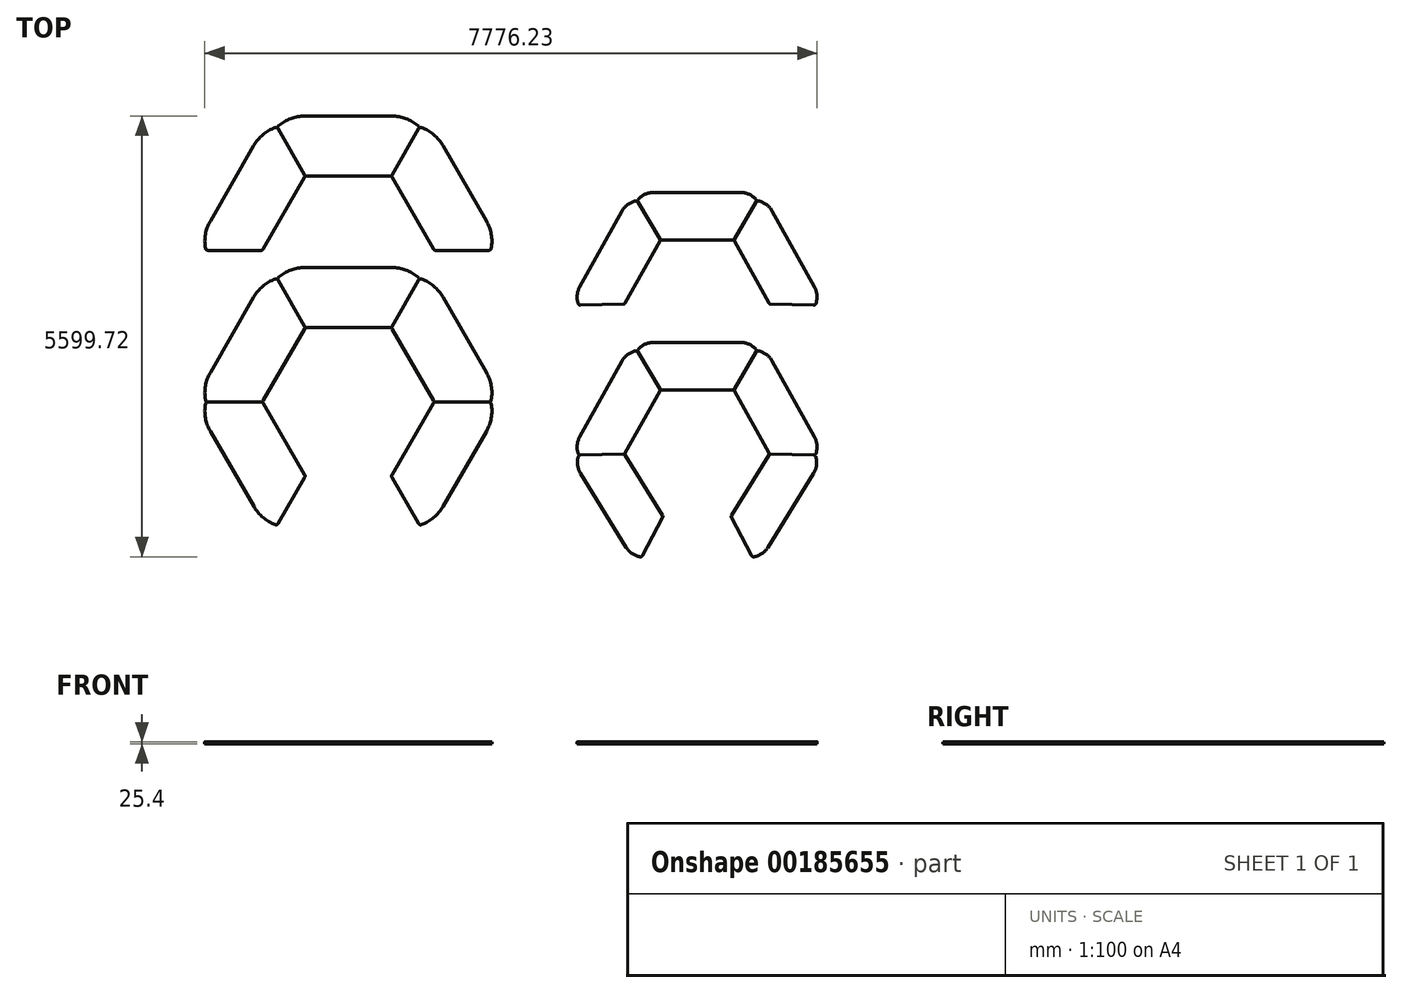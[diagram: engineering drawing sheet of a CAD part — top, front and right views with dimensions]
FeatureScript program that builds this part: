
annotation { "Feature Type Name" : "Feature", "Feature Type Description" : "" }
export const myFeature = defineFeature(function(context is Context, id is Id, definition is map)
    precondition{}
    {
        {
            var Q0;
            Q0=qCreatedBy(makeId("Top.planeOp"),FACE);
            var sketch = newSketch(context, id + "F0", { "sketchPlane" : qUnion([Q0])});
            skLineSegment(sketch, "E0", {"start": v(-1070.65, -55.75) * mm, "end": v(-16.67, -55.75) * mm});
            skLineSegment(sketch, "E1", {"start": v(-1436.4, 546.82) * mm, "end": v(-1097.33, -40.35) * mm});
            skLineSegment(sketch, "E2", {"start": v(10, -40.35) * mm, "end": v(349.27, 547.15) * mm});
            skLineSegment(sketch, "E3", {"start": v(-543.66, 584.33) * mm, "end": v(-543.66, -55.75) * mm});
            skPoint(sketch, "E4.visualSharp", {"position": v(-1088.43, -55.75) * mm});
            skArc(sketch, "E4.filletArc", {"start": v(-1097.33, -40.35) * mm, "mid": v(-1086.05, -51.62) * mm, "end": v(-1070.65, -55.75) * mm});
            skPoint(sketch, "E5.visualSharp", {"position": v(1.11, -55.75) * mm});
            skArc(sketch, "E5.filletArc", {"start": v(-16.67, -55.75) * mm, "mid": v(-1.27, -51.62) * mm, "end": v(10, -40.35) * mm});
            skLineSegment(sketch, "E6", {"start": v(-543.66, -55.75) * mm, "end": v(-543.66, 706.25) * mm});
            skPoint(sketch, "E7.visualSharp", {"position": v(8.73, 706.25) * mm});
            skLineSegment(sketch, "E8", {"start": v(-1096.05, 706.25) * mm, "end": v(8.73, 706.25) * mm});
            skArc(sketch, "E9", {"start": v(-1096.05, 706.25) * mm, "mid": v(-1273.45, 675.07) * mm, "end": v(-1429.58, 585.26) * mm});
            skArc(sketch, "E10", {"start": v(342.4, 585.63) * mm, "mid": v(186.13, 675.17) * mm, "end": v(8.73, 706.25) * mm});
            skPoint(sketch, "E11.visualSharp", {"position": v(361.73, 568.73) * mm});
            skArc(sketch, "E11.filletArc", {"start": v(349.27, 547.15) * mm, "mid": v(352.86, 567.65) * mm, "end": v(342.4, 585.63) * mm});
            skPoint(sketch, "E12.visualSharp", {"position": v(-1448.84, 568.35) * mm});
            skArc(sketch, "E12.filletArc", {"start": v(-1429.58, 585.26) * mm, "mid": v(-1440, 567.29) * mm, "end": v(-1436.4, 546.82) * mm});
            skSolve(sketch);
        }
        {
            var Q0;
            {var subQ1=sQuery(id+"F0.wireOp",EDGE,"E1");Q0=makeQuery(id+"F0.imprint","IMPRINT",FACE,{"disambiguationData":[TD([[makeQuery(id+"F0.imprint","IMPRINT",EDGE,{"derivedFrom":subQ1}),1.0]])]});}
            var Q1;
            {var subQ1=sQuery(id+"F0.wireOp",EDGE,"E2");Q1=makeQuery(id+"F0.imprint","IMPRINT",FACE,{"disambiguationData":[TD([[makeQuery(id+"F0.imprint","IMPRINT",EDGE,{"derivedFrom":subQ1}),1.0]])]});}
            extrude(context, id + "F1", {"entities" : qUnion([Q0, Q1]), "depth" : 25.4 * mm});
        }
        {
            var Q0;
            Q0=makeQuery(id+"F1.opExtrude","SWEPT_BODY",BODY,{"disambiguationData":[OSD([sQuery(id+"F0.wireOp",EDGE,"1ubpbm2j-zJwo-eIPi-8dKW-a2tcgGCZGCWk"),sQuery(id+"F0.wireOp",EDGE,"E0"),sQuery(id+"F0.wireOp",EDGE,"E1"),sQuery(id+"F0.wireOp",EDGE,"E2"),sQuery(id+"F0.wireOp",EDGE,"E4.filletArc"),sQuery(id+"F0.wireOp",EDGE,"E5.filletArc")])]});
            var Q1;
            Q1=makeQuery(id+"F1.opExtrude","SWEPT_FACE",FACE,{"disambiguationData":[OSD([sQuery(id+"F0.wireOp",EDGE,"E1")])]});
            mirror(context, id + "F2", {"entities" : qUnion([Q0]), "mirrorPlane" : qUnion([Q1])});
        }
        {
            var Q0;
            Q0=makeQuery(id+"F1.opExtrude","SWEPT_BODY",BODY,{"disambiguationData":[OSD([sQuery(id+"F0.wireOp",EDGE,"1ubpbm2j-zJwo-eIPi-8dKW-a2tcgGCZGCWk"),sQuery(id+"F0.wireOp",EDGE,"E0"),sQuery(id+"F0.wireOp",EDGE,"E1"),sQuery(id+"F0.wireOp",EDGE,"E2"),sQuery(id+"F0.wireOp",EDGE,"E4.filletArc"),sQuery(id+"F0.wireOp",EDGE,"E5.filletArc")])]});
            var Q1;
            Q1=makeQuery(id+"F1.opExtrude","SWEPT_FACE",FACE,{"disambiguationData":[OSD([sQuery(id+"F0.wireOp",EDGE,"E2")])]});
            mirror(context, id + "F3", {"entities" : qUnion([Q0]), "mirrorPlane" : qUnion([Q1])});
        }
        {
            var Q0;
            Q0=makeQuery(id+"F1.opExtrude","SWEPT_BODY",BODY,{"disambiguationData":[OSD([sQuery(id+"F0.wireOp",EDGE,"1ubpbm2j-zJwo-eIPi-8dKW-a2tcgGCZGCWk"),sQuery(id+"F0.wireOp",EDGE,"E0"),sQuery(id+"F0.wireOp",EDGE,"E1"),sQuery(id+"F0.wireOp",EDGE,"E2"),sQuery(id+"F0.wireOp",EDGE,"E4.filletArc"),sQuery(id+"F0.wireOp",EDGE,"E5.filletArc")])]});
            transform(context, id + "F4", {"entities" : qUnion([Q0]), "transformType" : TransformType.TRANSLATION_3D, "dx" : 0 * mm, "dy" : -1925.32 * mm, "dz" : 0 * mm, "makeCopy" : true});
        }
        {
            var Q0;
            Q0=makeQuery(id+"F4.opPattern","COPY",BODY,{"derivedFrom":makeQuery(id+"F1.opExtrude","SWEPT_BODY",BODY,{"disambiguationData":[OSD([sQuery(id+"F0.wireOp",EDGE,"1ubpbm2j-zJwo-eIPi-8dKW-a2tcgGCZGCWk"),sQuery(id+"F0.wireOp",EDGE,"E0"),sQuery(id+"F0.wireOp",EDGE,"E1"),sQuery(id+"F0.wireOp",EDGE,"E2"),sQuery(id+"F0.wireOp",EDGE,"E4.filletArc"),sQuery(id+"F0.wireOp",EDGE,"E5.filletArc")])]}),"instanceName":"1"});
            var Q1;
            Q1=makeQuery(id+"F4.opPattern","COPY",FACE,{"derivedFrom":makeQuery(id+"F1.opExtrude","SWEPT_FACE",FACE,{"disambiguationData":[OSD([sQuery(id+"F0.wireOp",EDGE,"E1")])]}),"instanceName":"1"});
            mirror(context, id + "F5", {"entities" : qUnion([Q0]), "mirrorPlane" : qUnion([Q1])});
        }
        {
            var Q0;
            Q0=makeQuery(id+"F5.opPattern","COPY",BODY,{"derivedFrom":makeQuery(id+"F4.opPattern","COPY",BODY,{"derivedFrom":makeQuery(id+"F1.opExtrude","SWEPT_BODY",BODY,{"disambiguationData":[OSD([sQuery(id+"F0.wireOp",EDGE,"1ubpbm2j-zJwo-eIPi-8dKW-a2tcgGCZGCWk"),sQuery(id+"F0.wireOp",EDGE,"E0"),sQuery(id+"F0.wireOp",EDGE,"E1"),sQuery(id+"F0.wireOp",EDGE,"E2"),sQuery(id+"F0.wireOp",EDGE,"E4.filletArc"),sQuery(id+"F0.wireOp",EDGE,"E5.filletArc")])]}),"instanceName":"1"}),"instanceName":"1"});
            var Q1;
            Q1=makeQuery(id+"F5.opPattern","COPY",FACE,{"derivedFrom":makeQuery(id+"F4.opPattern","COPY",FACE,{"derivedFrom":makeQuery(id+"F1.opExtrude","SWEPT_FACE",FACE,{"disambiguationData":[OSD([sQuery(id+"F0.wireOp",EDGE,"E2")])]}),"instanceName":"1"}),"instanceName":"1"});
            mirror(context, id + "F6", {"entities" : qUnion([Q0]), "mirrorPlane" : qUnion([Q1])});
        }
        {
            var Q0;
            Q0=qCreatedBy(makeId("Top.planeOp"),FACE);
            var sketch = newSketch(context, id + "F7", { "sketchPlane" : qUnion([Q0])});
            skLineSegment(sketch, "E13", {"start": v(3434.2, -869.87) * mm, "end": v(4337.07, -869.87) * mm});
            skLineSegment(sketch, "E14", {"start": v(3135.74, -386.36) * mm, "end": v(3412.3, -857.33) * mm});
            skLineSegment(sketch, "E15", {"start": v(4358.97, -857.33) * mm, "end": v(4635.53, -386.36) * mm});
            skPoint(sketch, "E16.visualSharp", {"position": v(3419.66, -869.87) * mm});
            skArc(sketch, "E16.filletArc", {"start": v(3412.3, -857.33) * mm, "mid": v(3421.58, -866.51) * mm, "end": v(3434.2, -869.87) * mm});
            skPoint(sketch, "E17.visualSharp", {"position": v(4351.6, -869.87) * mm});
            skArc(sketch, "E17.filletArc", {"start": v(4337.07, -869.87) * mm, "mid": v(4349.69, -866.51) * mm, "end": v(4358.97, -857.33) * mm});
            skLineSegment(sketch, "E18", {"start": v(3885.63, -365.75) * mm, "end": v(3885.63, -869.87) * mm});
            skLineSegment(sketch, "E19", {"start": v(3885.63, -869.87) * mm, "end": v(3885.63, -264.43) * mm});
            skLineSegment(sketch, "E20", {"start": v(3333.25, -264.43) * mm, "end": v(4438.02, -264.43) * mm});
            skArc(sketch, "E21", {"start": v(3333.25, -264.43) * mm, "mid": v(3227.14, -286.97) * mm, "end": v(3139.36, -350.7) * mm});
            skArc(sketch, "E22", {"start": v(4631.9, -350.7) * mm, "mid": v(4544.12, -286.97) * mm, "end": v(4438.02, -264.43) * mm});
            skPoint(sketch, "E23.visualSharp", {"position": v(3125, -368.08) * mm});
            skArc(sketch, "E23.filletArc", {"start": v(3139.36, -350.7) * mm, "mid": v(3131.72, -367.94) * mm, "end": v(3135.74, -386.36) * mm});
            skPoint(sketch, "E24.visualSharp", {"position": v(4646.26, -368.08) * mm});
            skArc(sketch, "E24.filletArc", {"start": v(4635.53, -386.36) * mm, "mid": v(4639.55, -367.94) * mm, "end": v(4631.9, -350.7) * mm});
            skSolve(sketch);
        }
        {
            var Q0;
            {var subQ1=sQuery(id+"F7.wireOp",EDGE,"E15");Q0=makeQuery(id+"F7.imprint","IMPRINT",FACE,{"disambiguationData":[TD([[makeQuery(id+"F7.imprint","IMPRINT",EDGE,{"derivedFrom":subQ1}),1.0]])]});}
            var Q1;
            {var subQ1=sQuery(id+"F7.wireOp",EDGE,"E14");Q1=makeQuery(id+"F7.imprint","IMPRINT",FACE,{"disambiguationData":[TD([[makeQuery(id+"F7.imprint","IMPRINT",EDGE,{"derivedFrom":subQ1}),1.0]])]});}
            extrude(context, id + "F8", {"entities" : qUnion([Q0, Q1]), "depth" : 25.4 * mm});
        }
        {
            var Q0;
            Q0=makeQuery(id+"F8.opExtrude","SWEPT_BODY",BODY,{"disambiguationData":[OSD([sQuery(id+"F7.wireOp",EDGE,"pXNZPhRm-cwQ2-fNh0-WMuh-DQMg4mvni5s0"),sQuery(id+"F7.wireOp",EDGE,"E13"),sQuery(id+"F7.wireOp",EDGE,"E14"),sQuery(id+"F7.wireOp",EDGE,"E15"),sQuery(id+"F7.wireOp",EDGE,"E16.filletArc"),sQuery(id+"F7.wireOp",EDGE,"E17.filletArc")])]});
            var Q1;
            Q1=makeQuery(id+"F8.opExtrude","SWEPT_FACE",FACE,{"disambiguationData":[OSD([sQuery(id+"F7.wireOp",EDGE,"E14")])]});
            mirror(context, id + "F9", {"entities" : qUnion([Q0]), "mirrorPlane" : qUnion([Q1])});
        }
        {
            var Q0;
            Q0=makeQuery(id+"F8.opExtrude","SWEPT_BODY",BODY,{"disambiguationData":[OSD([sQuery(id+"F7.wireOp",EDGE,"pXNZPhRm-cwQ2-fNh0-WMuh-DQMg4mvni5s0"),sQuery(id+"F7.wireOp",EDGE,"E13"),sQuery(id+"F7.wireOp",EDGE,"E14"),sQuery(id+"F7.wireOp",EDGE,"E15"),sQuery(id+"F7.wireOp",EDGE,"E16.filletArc"),sQuery(id+"F7.wireOp",EDGE,"E17.filletArc")])]});
            var Q1;
            Q1=makeQuery(id+"F8.opExtrude","SWEPT_FACE",FACE,{"disambiguationData":[OSD([sQuery(id+"F7.wireOp",EDGE,"E15")])]});
            mirror(context, id + "F10", {"entities" : qUnion([Q0]), "mirrorPlane" : qUnion([Q1])});
        }
        {
            var Q0;
            Q0=makeQuery(id+"F8.opExtrude","SWEPT_BODY",BODY,{"disambiguationData":[OSD([sQuery(id+"F7.wireOp",EDGE,"pXNZPhRm-cwQ2-fNh0-WMuh-DQMg4mvni5s0"),sQuery(id+"F7.wireOp",EDGE,"E13"),sQuery(id+"F7.wireOp",EDGE,"E14"),sQuery(id+"F7.wireOp",EDGE,"E15"),sQuery(id+"F7.wireOp",EDGE,"E16.filletArc"),sQuery(id+"F7.wireOp",EDGE,"E17.filletArc")])]});
            transform(context, id + "F11", {"entities" : qUnion([Q0]), "transformType" : TransformType.TRANSLATION_3D, "dx" : 0 * mm, "dy" : -1905 * mm, "dz" : 0 * mm, "makeCopy" : true});
        }
        {
            var Q0;
            Q0=makeQuery(id+"F11.opPattern","COPY",BODY,{"derivedFrom":makeQuery(id+"F8.opExtrude","SWEPT_BODY",BODY,{"disambiguationData":[OSD([sQuery(id+"F7.wireOp",EDGE,"pXNZPhRm-cwQ2-fNh0-WMuh-DQMg4mvni5s0"),sQuery(id+"F7.wireOp",EDGE,"E13"),sQuery(id+"F7.wireOp",EDGE,"E14"),sQuery(id+"F7.wireOp",EDGE,"E15"),sQuery(id+"F7.wireOp",EDGE,"E16.filletArc"),sQuery(id+"F7.wireOp",EDGE,"E17.filletArc")])]}),"instanceName":"1"});
            var Q1;
            Q1=makeQuery(id+"F11.opPattern","COPY",FACE,{"derivedFrom":makeQuery(id+"F8.opExtrude","SWEPT_FACE",FACE,{"disambiguationData":[OSD([sQuery(id+"F7.wireOp",EDGE,"E14")])]}),"instanceName":"1"});
            mirror(context, id + "F12", {"entities" : qUnion([Q0]), "mirrorPlane" : qUnion([Q1])});
        }
        {
            var Q0;
            Q0=makeQuery(id+"F12.opPattern","COPY",BODY,{"derivedFrom":makeQuery(id+"F11.opPattern","COPY",BODY,{"derivedFrom":makeQuery(id+"F8.opExtrude","SWEPT_BODY",BODY,{"disambiguationData":[OSD([sQuery(id+"F7.wireOp",EDGE,"pXNZPhRm-cwQ2-fNh0-WMuh-DQMg4mvni5s0"),sQuery(id+"F7.wireOp",EDGE,"E13"),sQuery(id+"F7.wireOp",EDGE,"E14"),sQuery(id+"F7.wireOp",EDGE,"E15"),sQuery(id+"F7.wireOp",EDGE,"E16.filletArc"),sQuery(id+"F7.wireOp",EDGE,"E17.filletArc")])]}),"instanceName":"1"}),"instanceName":"1"});
            var Q1;
            Q1=makeQuery(id+"F12.opPattern","COPY",FACE,{"derivedFrom":makeQuery(id+"F11.opPattern","COPY",FACE,{"derivedFrom":makeQuery(id+"F8.opExtrude","SWEPT_FACE",FACE,{"disambiguationData":[OSD([sQuery(id+"F7.wireOp",EDGE,"E15")])]}),"instanceName":"1"}),"instanceName":"1"});
            mirror(context, id + "F13", {"entities" : qUnion([Q0]), "mirrorPlane" : qUnion([Q1])});
        }
        {
            var Q0;
            Q0=makeQuery(id+"F4.opPattern","COPY",BODY,{"derivedFrom":makeQuery(id+"F1.opExtrude","SWEPT_BODY",BODY,{"disambiguationData":[OSD([sQuery(id+"F0.wireOp",EDGE,"1ubpbm2j-zJwo-eIPi-8dKW-a2tcgGCZGCWk"),sQuery(id+"F0.wireOp",EDGE,"E0"),sQuery(id+"F0.wireOp",EDGE,"E1"),sQuery(id+"F0.wireOp",EDGE,"E2"),sQuery(id+"F0.wireOp",EDGE,"E4.filletArc"),sQuery(id+"F0.wireOp",EDGE,"E5.filletArc")])]}),"instanceName":"1"});
            var Q1;
            Q1=makeQuery(id+"F4.opPattern","COPY",FACE,{"derivedFrom":makeQuery(id+"F1.opExtrude","SWEPT_FACE",FACE,{"disambiguationData":[OSD([sQuery(id+"F0.wireOp",EDGE,"E2")])]}),"instanceName":"1"});
            mirror(context, id + "F14", {"entities" : qUnion([Q0]), "mirrorPlane" : qUnion([Q1])});
        }
        {
            var Q0;
            Q0=makeQuery(id+"F11.opPattern","COPY",BODY,{"derivedFrom":makeQuery(id+"F8.opExtrude","SWEPT_BODY",BODY,{"disambiguationData":[OSD([sQuery(id+"F7.wireOp",EDGE,"pXNZPhRm-cwQ2-fNh0-WMuh-DQMg4mvni5s0"),sQuery(id+"F7.wireOp",EDGE,"E13"),sQuery(id+"F7.wireOp",EDGE,"E14"),sQuery(id+"F7.wireOp",EDGE,"E15"),sQuery(id+"F7.wireOp",EDGE,"E16.filletArc"),sQuery(id+"F7.wireOp",EDGE,"E17.filletArc")])]}),"instanceName":"1"});
            var Q1;
            Q1=makeQuery(id+"F11.opPattern","COPY",FACE,{"derivedFrom":makeQuery(id+"F8.opExtrude","SWEPT_FACE",FACE,{"disambiguationData":[OSD([sQuery(id+"F7.wireOp",EDGE,"E15")])]}),"instanceName":"1"});
            mirror(context, id + "F15", {"entities" : qUnion([Q0]), "mirrorPlane" : qUnion([Q1])});
        }
        {
            var Q0;
            Q0=makeQuery(id+"F15.opPattern","COPY",BODY,{"derivedFrom":makeQuery(id+"F11.opPattern","COPY",BODY,{"derivedFrom":makeQuery(id+"F8.opExtrude","SWEPT_BODY",BODY,{"disambiguationData":[OSD([sQuery(id+"F7.wireOp",EDGE,"E13"),sQuery(id+"F7.wireOp",EDGE,"E14"),sQuery(id+"F7.wireOp",EDGE,"E15"),sQuery(id+"F7.wireOp",EDGE,"E16.filletArc"),sQuery(id+"F7.wireOp",EDGE,"E17.filletArc"),sQuery(id+"F7.wireOp",EDGE,"E20"),sQuery(id+"F7.wireOp",EDGE,"E21"),sQuery(id+"F7.wireOp",EDGE,"E22"),sQuery(id+"F7.wireOp",EDGE,"E23.filletArc"),sQuery(id+"F7.wireOp",EDGE,"E24.filletArc")])]}),"instanceName":"1"}),"instanceName":"1"});
            var Q1;
            Q1=makeQuery(id+"F15.opPattern","COPY",FACE,{"derivedFrom":makeQuery(id+"F11.opPattern","COPY",FACE,{"derivedFrom":makeQuery(id+"F8.opExtrude","SWEPT_FACE",FACE,{"disambiguationData":[OSD([sQuery(id+"F7.wireOp",EDGE,"E14")])]}),"instanceName":"1"}),"instanceName":"1"});
            mirror(context, id + "F16", {"entities" : qUnion([Q0]), "mirrorPlane" : qUnion([Q1])});
        }
        {
            var Q0;
            Q0=makeQuery(id+"F14.opPattern","COPY",BODY,{"derivedFrom":makeQuery(id+"F4.opPattern","COPY",BODY,{"derivedFrom":makeQuery(id+"F1.opExtrude","SWEPT_BODY",BODY,{"disambiguationData":[OSD([sQuery(id+"F0.wireOp",EDGE,"1ubpbm2j-zJwo-eIPi-8dKW-a2tcgGCZGCWk"),sQuery(id+"F0.wireOp",EDGE,"E0"),sQuery(id+"F0.wireOp",EDGE,"E1"),sQuery(id+"F0.wireOp",EDGE,"E2"),sQuery(id+"F0.wireOp",EDGE,"E4.filletArc"),sQuery(id+"F0.wireOp",EDGE,"E5.filletArc")])]}),"instanceName":"1"}),"instanceName":"1"});
            var Q1;
            Q1=makeQuery(id+"F14.opPattern","COPY",FACE,{"derivedFrom":makeQuery(id+"F4.opPattern","COPY",FACE,{"derivedFrom":makeQuery(id+"F1.opExtrude","SWEPT_FACE",FACE,{"disambiguationData":[OSD([sQuery(id+"F0.wireOp",EDGE,"E1")])]}),"instanceName":"1"}),"instanceName":"1"});
            mirror(context, id + "F17", {"entities" : qUnion([Q0]), "mirrorPlane" : qUnion([Q1])});
        }
    });
